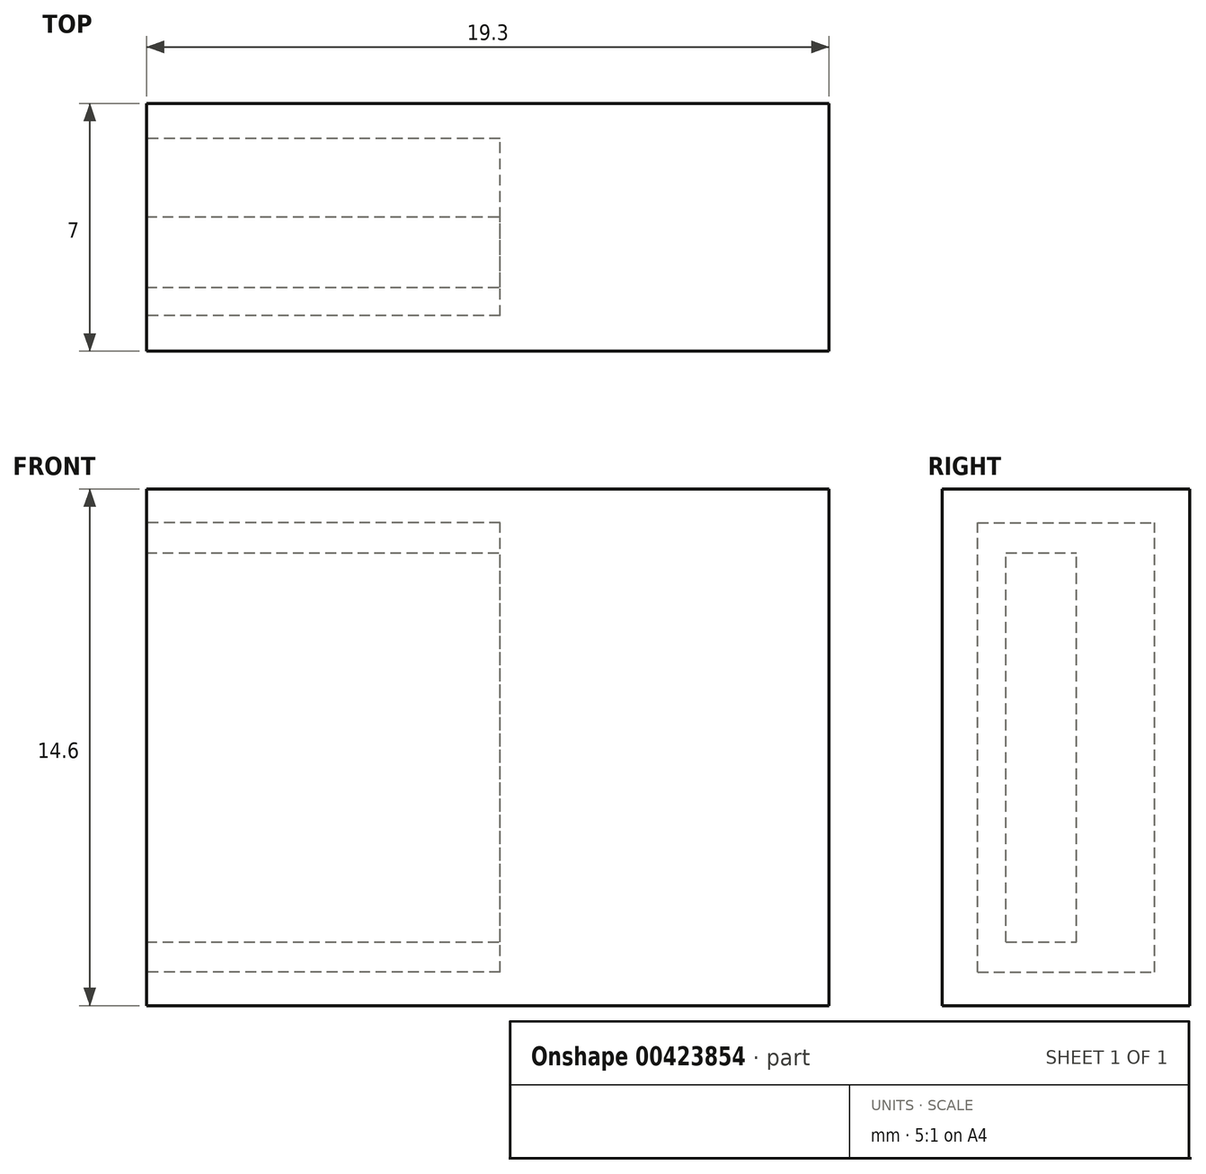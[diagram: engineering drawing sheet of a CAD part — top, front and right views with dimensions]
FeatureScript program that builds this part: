
annotation { "Feature Type Name" : "Feature", "Feature Type Description" : "" }
export const myFeature = defineFeature(function(context is Context, id is Id, definition is map)
    precondition{}
    {
        {
            var Q0;
            Q0=qCreatedBy(makeId("Front.planeOp"),FACE);
            var sketch = newSketch(context, id + "F0", { "sketchPlane" : qUnion([Q0])});
            skLineSegment(sketch, "E0.bottom", {"start": v(0, 0) * mm, "end": v(19.3, 0) * mm});
            skLineSegment(sketch, "E0.top", {"start": v(0, 14.6) * mm, "end": v(19.3, 14.6) * mm});
            skLineSegment(sketch, "E0.left", {"start": v(0, 0) * mm, "end": v(0, 14.6) * mm});
            skLineSegment(sketch, "E0.right", {"start": v(19.3, 0) * mm, "end": v(19.3, 14.6) * mm});
            skSolve(sketch);
        }
        {
            var Q0;
            Q0=qSketchRegion(id+"F0",true);
            extrude(context, id + "F1", {"entities" : qUnion([Q0]), "depth" : 7 * mm});
        }
        {
            var Q0;
            Q0=makeQuery(id+"F1.opExtrude","SWEPT_FACE",FACE,{"disambiguationData":[OSD([sQuery(id+"F0.wireOp",EDGE,"E0.left")])]});
            var sketch = newSketch(context, id + "F2", { "sketchPlane" : qUnion([Q0])});
            skLineSegment(sketch, "E1.bottom", {"start": v(6, 0.95) * mm, "end": v(1, 0.95) * mm});
            skLineSegment(sketch, "E1.top", {"start": v(6, 13.65) * mm, "end": v(1, 13.65) * mm});
            skLineSegment(sketch, "E1.left", {"start": v(6, 0.95) * mm, "end": v(6, 13.65) * mm});
            skLineSegment(sketch, "E1.right", {"start": v(1, 0.95) * mm, "end": v(1, 13.65) * mm});
            skPoint(sketch, "E1.middle", {"position": v(3.5, 7.3) * mm});
            skPoint(sketch, "E1.middle.positionSnap0", {"position": v(3.5, 14.6) * mm});
            skPoint(sketch, "E1.middle.positionSnap1", {"position": v(0, 7.3) * mm});
            skPoint(sketch, "E1.centerSnap0", {"position": v(3.5, 14.6) * mm});
            skPoint(sketch, "E1.centerSnap1", {"position": v(0, 7.3) * mm});
            skSolve(sketch);
        }
        {
            var Q0;
            Q0=qSketchRegion(id+"F2",true);
            extrude(context, id + "F3", {"entities" : qUnion([Q0]), "operationType" : NewBodyOperationType.REMOVE, "oppositeDirection" : true, "depth" : 10 * mm});
        }
        {
            var Q0;
            Q0=makeQuery(id+"F3.boolean.opBoolean","COPY",FACE,{"derivedFrom":makeQuery(id+"F3.opExtrude","CAP_FACE",FACE,{"disambiguationData":[OSD([sQuery(id+"F2.wireOp",EDGE,"E1.bottom"),sQuery(id+"F2.wireOp",EDGE,"E1.top"),sQuery(id+"F2.wireOp",EDGE,"E1.left"),sQuery(id+"F2.wireOp",EDGE,"E1.right")])],"isStart":false})});
            var sketch = newSketch(context, id + "F4", { "sketchPlane" : qUnion([Q0])});
            skLineSegment(sketch, "E2.bottom", {"start": v(5.2, 1.8) * mm, "end": v(3.2, 1.8) * mm});
            skLineSegment(sketch, "E2.top", {"start": v(5.2, 12.8) * mm, "end": v(3.2, 12.8) * mm});
            skLineSegment(sketch, "E2.left", {"start": v(5.2, 1.8) * mm, "end": v(5.2, 12.8) * mm});
            skLineSegment(sketch, "E2.right", {"start": v(3.2, 1.8) * mm, "end": v(3.2, 12.8) * mm});
            skPoint(sketch, "E2.middle", {"position": v(4.2, 7.3) * mm});
            skPoint(sketch, "E2.middle.positionSnap0", {"position": v(6, 7.3) * mm});
            skPoint(sketch, "E2.centerSnap0", {"position": v(6, 7.3) * mm});
            skSolve(sketch);
        }
        {
            var Q0;
            Q0=qSketchRegion(id+"F4",true);
            extrude(context, id + "F5", {"entities" : qUnion([Q0]), "operationType" : NewBodyOperationType.ADD, "depth" : 10 * mm});
        }
    });
